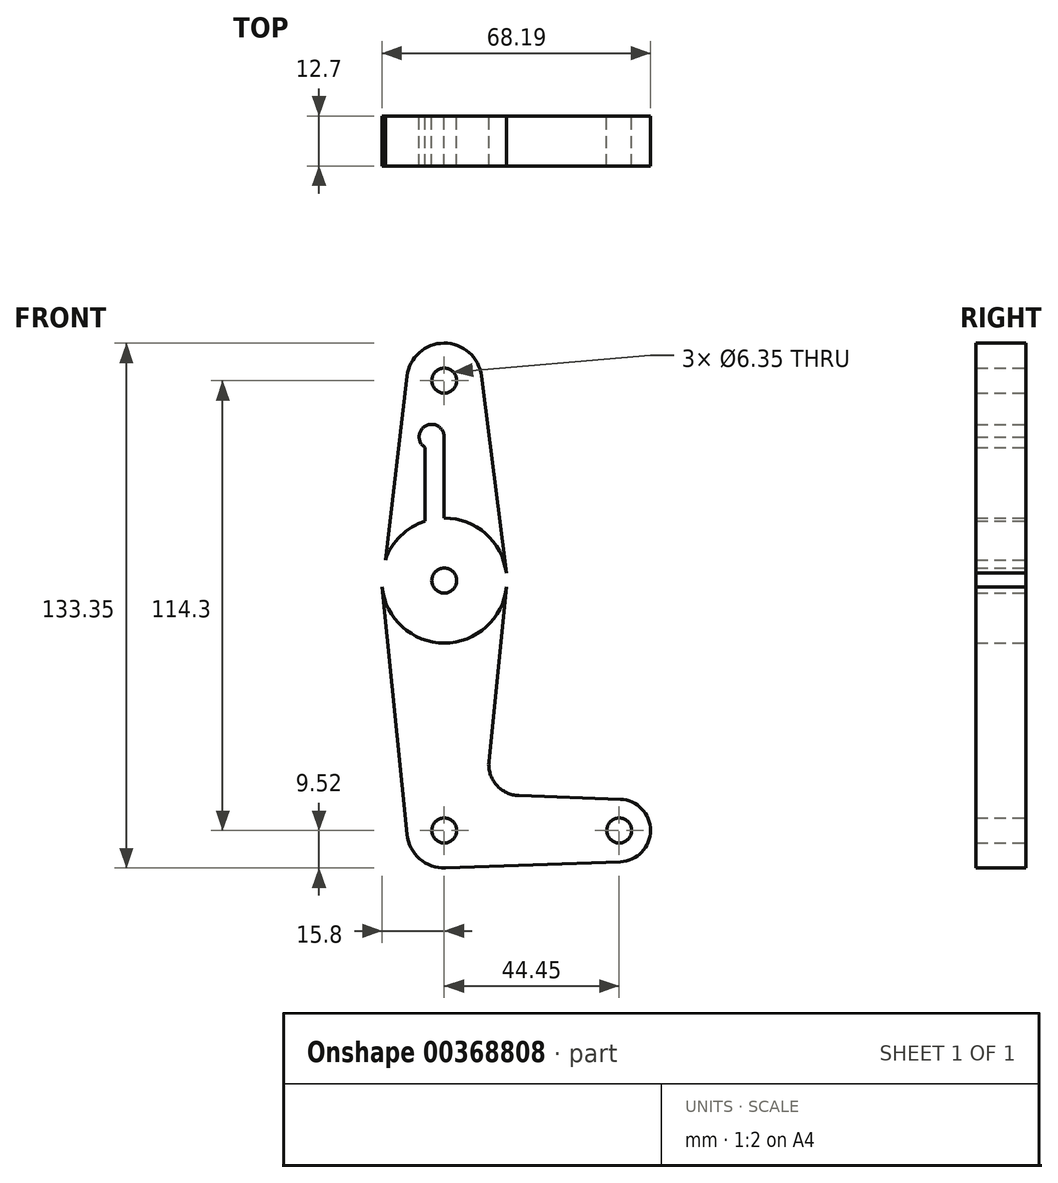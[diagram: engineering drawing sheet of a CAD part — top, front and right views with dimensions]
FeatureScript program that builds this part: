
annotation { "Feature Type Name" : "Feature", "Feature Type Description" : "" }
export const myFeature = defineFeature(function(context is Context, id is Id, definition is map)
    precondition{}
    {
        {
            var Q0;
            Q0=qCreatedBy(makeId("Front.planeOp"),FACE);
            var sketch = newSketch(context, id + "F0", { "sketchPlane" : qUnion([Q0])});
            skLineSegment(sketch, "E0", {"start": v(0, 0) * mm, "end": v(0, 114.3) * mm});
            skLineSegment(sketch, "E1", {"start": v(0, 0) * mm, "end": v(44.45, 0) * mm});
            skCircle(sketch, "E2", {"center": v(0, 63.5) * mm, "radius": 15.88 * mm});
            skLineSegment(sketch, "E3", {"start": v(0, 63.5) * mm, "end": v(0, 0) * mm});
            skCircle(sketch, "E4", {"center": v(0, 114.3) * mm, "radius": 9.53 * mm});
            skCircle(sketch, "E5", {"center": v(0, 0) * mm, "radius": 9.53 * mm});
            skCircle(sketch, "E6", {"center": v(44.45, 0) * mm, "radius": 7.94 * mm});
            skLineSegment(sketch, "E7", {"start": v(9.45, 115.5) * mm, "end": v(15.75, 65.48) * mm});
            skLineSegment(sketch, "E8", {"start": v(-9.46, 115.42) * mm, "end": v(-15.8, 61.91) * mm});
            skLineSegment(sketch, "E9", {"start": v(0.34, -9.52) * mm, "end": v(44.73, -7.93) * mm});
            skLineSegment(sketch, "E10", {"start": v(15.8, 61.91) * mm, "end": v(11.34, 17.6) * mm});
            skLineSegment(sketch, "E11", {"start": v(44.73, 7.93) * mm, "end": v(18.97, 8.85) * mm});
            skLineSegment(sketch, "E12", {"start": v(-15.8, 61.91) * mm, "end": v(-9.48, -0.95) * mm});
            skArc(sketch, "E13.filletArc", {"start": v(11.34, 17.6) * mm, "mid": v(13.26, 11.57) * mm, "end": v(18.97, 8.85) * mm});
            skCircle(sketch, "E14", {"center": v(0, 0) * mm, "radius": 3.18 * mm});
            skCircle(sketch, "E15", {"center": v(44.45, 0) * mm, "radius": 3.18 * mm});
            skCircle(sketch, "E16", {"center": v(0, 63.5) * mm, "radius": 3.18 * mm});
            skCircle(sketch, "E17", {"center": v(0, 114.3) * mm, "radius": 3.18 * mm});
            skLineSegment(sketch, "E18", {"start": v(0, 89.56) * mm, "end": v(-3.18, 89.56) * mm});
            skLineSegment(sketch, "E19", {"start": v(-4.84, 63.5) * mm, "end": v(-4.84, 100.03) * mm});
            skLineSegment(sketch, "E20", {"start": v(-4.84, 100.03) * mm, "end": v(0, 100.03) * mm});
            skCircle(sketch, "E21", {"center": v(-3.21, 100.03) * mm, "radius": 3.18 * mm});
            skSolve(sketch);
        }
        {
            var Q0;
            {var subQ4=sQuery(id+"F0.wireOp",EDGE,"E7");Q0=makeQuery(id+"F0.imprint","IMPRINT",FACE,{"disambiguationData":[TD([[makeQuery(id+"F0.imprint","IMPRINT",EDGE,{"derivedFrom":subQ4}),-1.0]])]});}
            var Q1;
            Q1=makeQuery(id+"F0.imprint","IMPRINT",FACE,{"disambiguationData":[TD([[makeQuery(id+"F0.imprint","IMPRINT",EDGE,{"derivedFrom":sQuery(id+"F0.wireOp",EDGE,"E17")}),-1.0]])]});
            var Q2;
            {var subQ5=sQuery(id+"F0.wireOp",EDGE,"E0");var subQ9=sQuery(id+"F0.wireOp",EDGE,"E20");var subQ10=makeQuery(id+"F0.imprint","INTERSECT",VERTEX,{"derivedFrom":[subQ5,subQ9]});Q2=makeQuery(id+"F0.imprint","IMPRINT",FACE,{"disambiguationData":[TD([[makeQuery(id+"F0.imprint","IMPRINT",EDGE,{"disambiguationData":[TD([[subQ10,-1.0]])],"derivedFrom":subQ5}),1.0]])]});}
            var Q3;
            {var subQ5=sQuery(id+"F0.wireOp",EDGE,"E0");var subQ7=makeQuery(id+"F0.imprint","IMPRINT",VERTEX,{"derivedFrom":subQ5});Q3=makeQuery(id+"F0.imprint","IMPRINT",FACE,{"disambiguationData":[TD([[makeQuery(id+"F0.imprint","IMPRINT",EDGE,{"disambiguationData":[TD([[subQ7,1.0]])],"derivedFrom":subQ5}),1.0]])]});}
            var Q4;
            {var subQ5=sQuery(id+"F0.wireOp",EDGE,"E16");var subQ6=sQuery(id+"F0.wireOp",EDGE,"E0");var subQ7=makeQuery(id+"F0.imprint","INTERSECT",VERTEX,{"derivedFrom":[subQ6,subQ5]});Q4=makeQuery(id+"F0.imprint","IMPRINT",FACE,{"disambiguationData":[TD([[makeQuery(id+"F0.imprint","IMPRINT",EDGE,{"disambiguationData":[TD([[subQ7,-1.0]])],"derivedFrom":subQ6}),1.0]])]});}
            var Q5;
            {var subQ5=sQuery(id+"F0.wireOp",EDGE,"E0");var subQ7=sQuery(id+"F0.wireOp",EDGE,"E16");var subQ8=makeQuery(id+"F0.imprint","INTERSECT",VERTEX,{"derivedFrom":[subQ5,subQ7]});Q5=makeQuery(id+"F0.imprint","IMPRINT",FACE,{"disambiguationData":[TD([[makeQuery(id+"F0.imprint","IMPRINT",EDGE,{"disambiguationData":[TD([[subQ8,-1.0]])],"derivedFrom":subQ5}),-1.0]])]});}
            var Q6;
            {var subQ5=sQuery(id+"F0.wireOp",EDGE,"E10");Q6=makeQuery(id+"F0.imprint","IMPRINT",FACE,{"disambiguationData":[TD([[makeQuery(id+"F0.imprint","IMPRINT",EDGE,{"derivedFrom":subQ5}),-1.0]])]});}
            var Q7;
            {var subQ0=sQuery(id+"F0.wireOp",EDGE,"E12");Q7=makeQuery(id+"F0.imprint","IMPRINT",FACE,{"disambiguationData":[TD([[makeQuery(id+"F0.imprint","IMPRINT",EDGE,{"derivedFrom":subQ0}),1.0]])]});}
            var Q8;
            {var subQ5=sQuery(id+"F0.wireOp",EDGE,"E14");var subQ7=sQuery(id+"F0.wireOp",EDGE,"E1");var subQ8=makeQuery(id+"F0.imprint","INTERSECT",VERTEX,{"derivedFrom":[subQ7,subQ5]});Q8=makeQuery(id+"F0.imprint","IMPRINT",FACE,{"disambiguationData":[TD([[makeQuery(id+"F0.imprint","IMPRINT",EDGE,{"disambiguationData":[TD([[subQ8,-1.0]])],"derivedFrom":subQ7}),-1.0]])]});}
            var Q9;
            {var subQ0=sQuery(id+"F0.wireOp",EDGE,"E14");var subQ1=sQuery(id+"F0.wireOp",EDGE,"E1");var subQ2=makeQuery(id+"F0.imprint","INTERSECT",VERTEX,{"derivedFrom":[subQ1,subQ0]});Q9=makeQuery(id+"F0.imprint","IMPRINT",FACE,{"disambiguationData":[TD([[makeQuery(id+"F0.imprint","IMPRINT",EDGE,{"disambiguationData":[TD([[subQ2,-1.0]])],"derivedFrom":subQ1}),1.0]])]});}
            var Q10;
            {var subQ5=sQuery(id+"F0.wireOp",EDGE,"E9");Q10=makeQuery(id+"F0.imprint","IMPRINT",FACE,{"disambiguationData":[TD([[makeQuery(id+"F0.imprint","IMPRINT",EDGE,{"derivedFrom":subQ5}),1.0]])]});}
            var Q11;
            Q11=makeQuery(id+"F0.imprint","IMPRINT",FACE,{"disambiguationData":[TD([[makeQuery(id+"F0.imprint","IMPRINT",EDGE,{"derivedFrom":sQuery(id+"F0.wireOp",EDGE,"E15")}),-1.0]])]});
            extrude(context, id + "F1", {"entities" : qUnion([Q0, Q1, Q2, Q3, Q4, Q5, Q6, Q7, Q8, Q9, Q10, Q11]), "depth" : 12.7 * mm});
        }
    });
